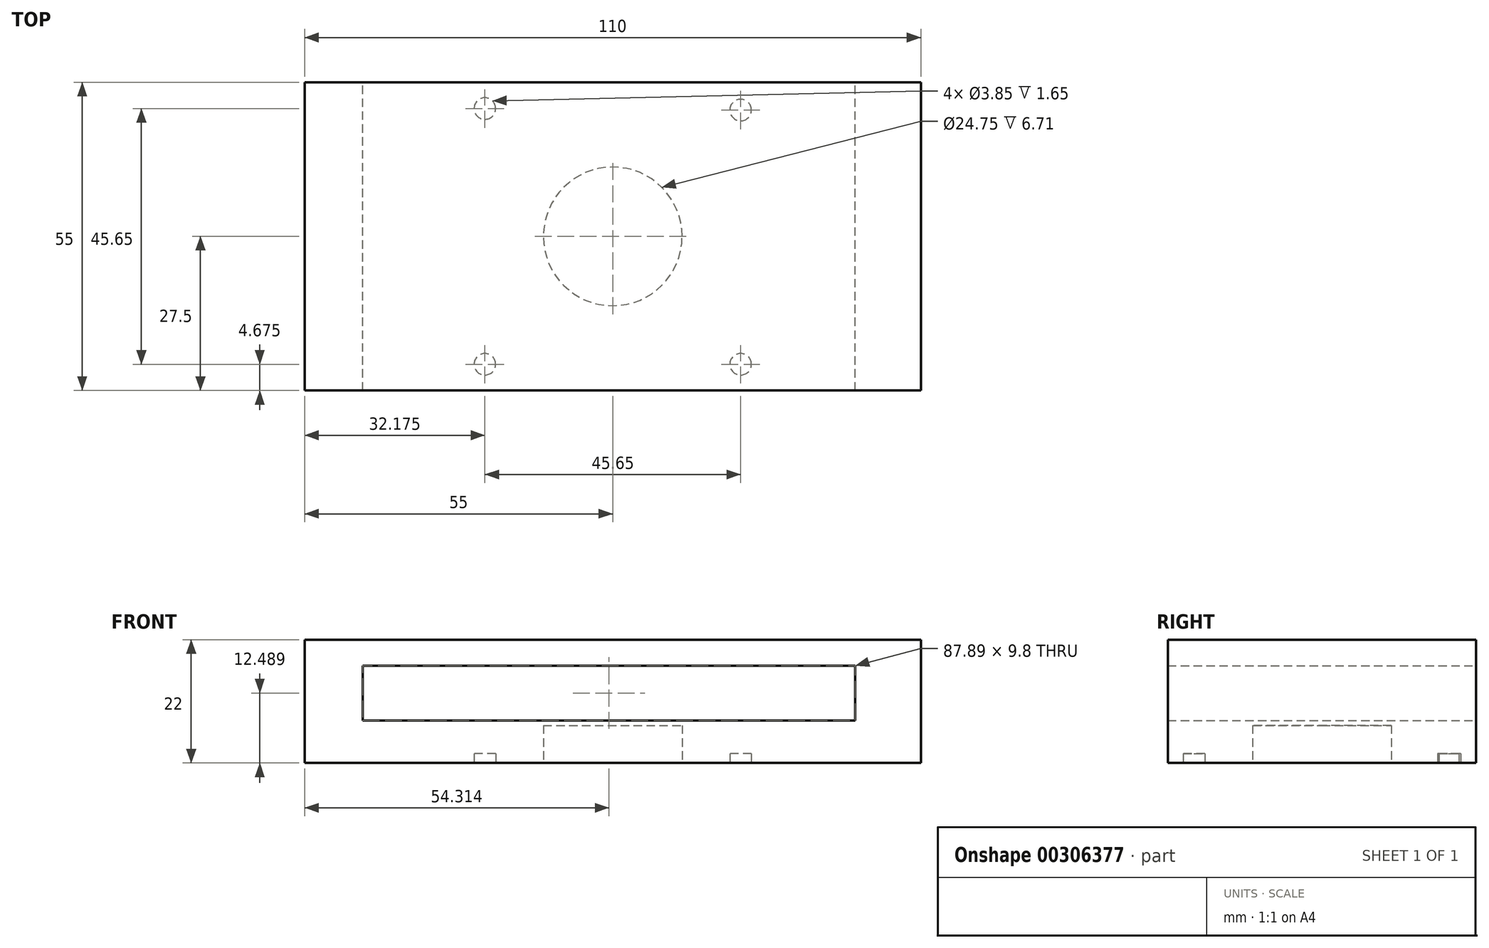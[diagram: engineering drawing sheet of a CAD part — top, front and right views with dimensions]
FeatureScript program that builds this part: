
annotation { "Feature Type Name" : "Feature", "Feature Type Description" : "" }
export const myFeature = defineFeature(function(context is Context, id is Id, definition is map)
    precondition{}
    {
        {
            var Q0;
            Q0=qCreatedBy(makeId("Front.planeOp"),FACE);
            var sketch = newSketch(context, id + "F0", { "sketchPlane" : qUnion([Q0])});
            skLineSegment(sketch, "E0.bottom", {"start": v(0, 0) * mm, "end": v(-2000, 0) * mm});
            skLineSegment(sketch, "E0.top", {"start": v(0, 425) * mm, "end": v(-2000, 425) * mm});
            skLineSegment(sketch, "E0.left", {"start": v(0, 0) * mm, "end": v(0, 425) * mm});
            skLineSegment(sketch, "E0.right", {"start": v(-2000, 0) * mm, "end": v(-2000, 425) * mm});
            skLineSegment(sketch, "E1.bottom", {"start": v(-1811.49, 316.17) * mm, "end": v(-213.45, 316.17) * mm});
            skLineSegment(sketch, "E1.top", {"start": v(-1811.49, 137.98) * mm, "end": v(-213.45, 137.98) * mm});
            skLineSegment(sketch, "E1.left", {"start": v(-1811.49, 316.17) * mm, "end": v(-1811.49, 137.98) * mm});
            skLineSegment(sketch, "E1.right", {"start": v(-213.45, 316.17) * mm, "end": v(-213.45, 137.98) * mm});
            skSolve(sketch);
        }
        {
            var Q0;
            Q0=makeQuery(id+"F0.imprint","IMPRINT",FACE,{"disambiguationData":[TD([[makeQuery(id+"F0.imprint","IMPRINT",EDGE,{"derivedFrom":sQuery(id+"F0.wireOp",EDGE,"E0.bottom")}),-1.0]])]});
            extrude(context, id + "F1", {"entities" : qUnion([Q0]), "depth" : 1000 * mm});
        }
        {
            var Q0;
            Q0=makeQuery(id+"F1.opExtrude","SWEPT_FACE",FACE,{"disambiguationData":[OSD([sQuery(id+"F0.wireOp",EDGE,"E0.top")])]});
            extrude(context, id + "F2", {"entities" : qUnion([Q0]), "operationType" : NewBodyOperationType.REMOVE, "oppositeDirection" : true, "depth" : 25 * mm});
        }
        {
            var Q0;
            Q0=qCreatedBy(makeId("Top.planeOp"),FACE);
            var sketch = newSketch(context, id + "F3", { "sketchPlane" : qUnion([Q0])});
            skCircle(sketch, "E2", {"center": v(-1415, -85) * mm, "radius": 35 * mm});
            skCircle(sketch, "E3", {"center": v(-585, -90) * mm, "radius": 35 * mm});
            skCircle(sketch, "E4", {"center": v(-1415, -915) * mm, "radius": 35 * mm});
            skCircle(sketch, "E5", {"center": v(-585, -915) * mm, "radius": 35 * mm});
            skSolve(sketch);
        }
        {
            var Q0;
            Q0=makeQuery(id+"F3.imprint","IMPRINT",FACE,{"disambiguationData":[TD([[makeQuery(id+"F3.imprint","IMPRINT",EDGE,{"derivedFrom":sQuery(id+"F3.wireOp",EDGE,"E2")}),1.0]])]});
            var Q1;
            Q1=makeQuery(id+"F3.imprint","IMPRINT",FACE,{"disambiguationData":[TD([[makeQuery(id+"F3.imprint","IMPRINT",EDGE,{"derivedFrom":sQuery(id+"F3.wireOp",EDGE,"E4")}),1.0]])]});
            var Q2;
            Q2=makeQuery(id+"F3.imprint","IMPRINT",FACE,{"disambiguationData":[TD([[makeQuery(id+"F3.imprint","IMPRINT",EDGE,{"derivedFrom":sQuery(id+"F3.wireOp",EDGE,"E5")}),1.0]])]});
            var Q3;
            Q3=makeQuery(id+"F3.imprint","IMPRINT",FACE,{"disambiguationData":[TD([[makeQuery(id+"F3.imprint","IMPRINT",EDGE,{"derivedFrom":sQuery(id+"F3.wireOp",EDGE,"E3")}),1.0]])]});
            extrude(context, id + "F4", {"entities" : qUnion([Q0, Q1, Q2, Q3]), "operationType" : NewBodyOperationType.REMOVE, "depth" : 30 * mm});
        }
        {
            var Q0;
            Q0=makeQuery(id+"F1.opExtrude","SWEPT_FACE",FACE,{"disambiguationData":[OSD([sQuery(id+"F0.wireOp",EDGE,"E0.bottom")])]});
            var sketch = newSketch(context, id + "F5", { "sketchPlane" : qUnion([Q0])});
            skCircle(sketch, "E6", {"center": v(-1000, 500) * mm, "radius": 225 * mm});
            skSolve(sketch);
        }
        {
            var Q0;
            Q0=makeQuery(id+"F5.imprint","IMPRINT",FACE,{"disambiguationData":[TD([[makeQuery(id+"F5.imprint","IMPRINT",EDGE,{"derivedFrom":sQuery(id+"F5.wireOp",EDGE,"E6")}),1.0]])]});
            extrude(context, id + "F6", {"entities" : qUnion([Q0]), "operationType" : NewBodyOperationType.REMOVE, "oppositeDirection" : true, "depth" : 122 * mm});
        }
        {
            var Q0;
            Q0=makeQuery(id+"F1.opExtrude","SWEPT_BODY",BODY,{"disambiguationData":[OSD([sQuery(id+"F0.wireOp",EDGE,"E0.bottom"),sQuery(id+"F0.wireOp",EDGE,"E0.top"),sQuery(id+"F0.wireOp",EDGE,"E0.left"),sQuery(id+"F0.wireOp",EDGE,"E0.right"),sQuery(id+"F0.wireOp",EDGE,"E1.bottom"),sQuery(id+"F0.wireOp",EDGE,"E1.top"),sQuery(id+"F0.wireOp",EDGE,"E1.left"),sQuery(id+"F0.wireOp",EDGE,"E1.right")])]});
            var Q1;
            Q1=qCreatedBy(makeId("Origin.pointOp"),VERTEX);
            transform(context, id + "F7", {"entities" : qUnion([Q0]), "transformType" : TransformType.SCALE_UNIFORMLY, "scale" : 0.06, "scalePoint" : qUnion([Q1]), "makeCopy" : false});
        }
    });
